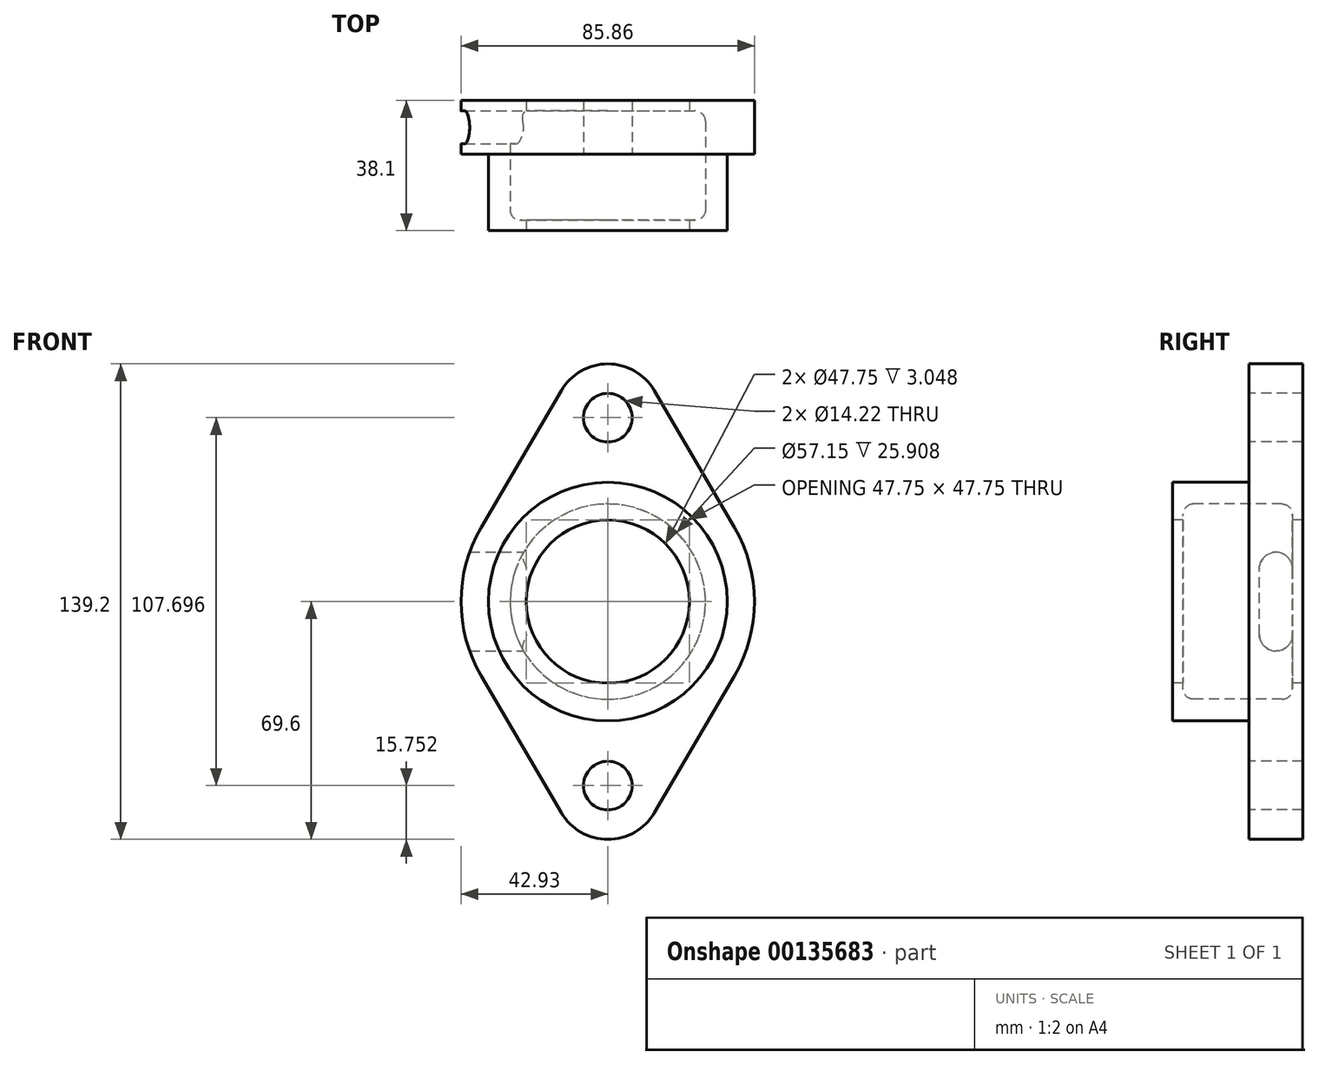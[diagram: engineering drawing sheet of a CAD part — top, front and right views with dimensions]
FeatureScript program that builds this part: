
annotation { "Feature Type Name" : "Feature", "Feature Type Description" : "" }
export const myFeature = defineFeature(function(context is Context, id is Id, definition is map)
    precondition{}
    {
        {
            var Q0;
            Q0=qCreatedBy(makeId("Front.planeOp"),FACE);
            var sketch = newSketch(context, id + "F0", { "sketchPlane" : qUnion([Q0])});
            skArc(sketch, "E0", {"start": v(37.06, -21.67) * mm, "mid": v(42.93, 0) * mm, "end": v(37.06, 21.67) * mm});
            skArc(sketch, "E1", {"start": v(-37.06, 21.67) * mm, "mid": v(-42.93, 0) * mm, "end": v(-37.06, -21.67) * mm});
            skLineSegment(sketch, "E2", {"start": v(-37.06, 21.67) * mm, "end": v(-13.6, 61.8) * mm});
            skLineSegment(sketch, "E3", {"start": v(-37.06, -21.67) * mm, "end": v(-13.6, -61.8) * mm});
            skLineSegment(sketch, "E4", {"start": v(37.06, 21.67) * mm, "end": v(13.6, 61.8) * mm});
            skLineSegment(sketch, "E5", {"start": v(37.06, -21.67) * mm, "end": v(13.6, -61.8) * mm});
            skArc(sketch, "E6", {"start": v(13.6, 61.8) * mm, "mid": v(0, 69.6) * mm, "end": v(-13.6, 61.8) * mm});
            skArc(sketch, "E7", {"start": v(-13.6, -61.8) * mm, "mid": v(0, -69.6) * mm, "end": v(13.6, -61.8) * mm});
            skCircle(sketch, "E8", {"center": v(0, 53.85) * mm, "radius": 7.11 * mm});
            skCircle(sketch, "E9", {"center": v(0, -53.85) * mm, "radius": 7.11 * mm});
            skSolve(sketch);
        }
        {
            var Q0;
            Q0=qSketchRegion(id+"F0",true);
            extrude(context, id + "F1", {"entities" : qUnion([Q0]), "oppositeDirection" : true, "depth" : 15.75 * mm});
        }
        {
            var Q0;
            Q0=makeQuery(id+"F1.opExtrude","CAP_FACE",FACE,{"disambiguationData":[OSD([sQuery(id+"F0.wireOp",EDGE,"E0"),sQuery(id+"F0.wireOp",EDGE,"E1"),sQuery(id+"F0.wireOp",EDGE,"E2"),sQuery(id+"F0.wireOp",EDGE,"E3"),sQuery(id+"F0.wireOp",EDGE,"E4"),sQuery(id+"F0.wireOp",EDGE,"E5"),sQuery(id+"F0.wireOp",EDGE,"E6"),sQuery(id+"F0.wireOp",EDGE,"E7"),sQuery(id+"F0.wireOp",EDGE,"E8"),sQuery(id+"F0.wireOp",EDGE,"E9")])],"isStart":true});
            var sketch = newSketch(context, id + "F2", { "sketchPlane" : qUnion([Q0])});
            skCircle(sketch, "E10", {"center": v(0, 0) * mm, "radius": 34.93 * mm});
            skSolve(sketch);
        }
        {
            var Q0;
            Q0=qSketchRegion(id+"F2",true);
            extrude(context, id + "F3", {"entities" : qUnion([Q0]), "operationType" : NewBodyOperationType.ADD, "depth" : 22.35 * mm});
        }
        {
            var Q0;
            Q0=qCreatedBy(makeId("Top.planeOp"),FACE);
            var sketch = newSketch(context, id + "F4", { "sketchPlane" : qUnion([Q0])});
            skLineSegment(sketch, "E11.bottom", {"start": v(-25.53, 12.7) * mm, "end": v(0, 12.7) * mm});
            skLineSegment(sketch, "E11.top", {"start": v(-25.53, -19.3) * mm, "end": v(0, -19.3) * mm});
            skLineSegment(sketch, "E11.left", {"start": v(-28.57, 9.65) * mm, "end": v(-28.57, -16.26) * mm});
            skPoint(sketch, "E12.visualSharp", {"position": v(-28.57, 12.7) * mm});
            skArc(sketch, "E12.filletArc", {"start": v(-25.53, 12.7) * mm, "mid": v(-27.68, 11.8) * mm, "end": v(-28.58, 9.65) * mm});
            skPoint(sketch, "E13.visualSharp", {"position": v(-28.57, -19.3) * mm});
            skArc(sketch, "E13.filletArc", {"start": v(-28.57, -16.26) * mm, "mid": v(-27.68, -18.41) * mm, "end": v(-25.53, -19.3) * mm});
            skLineSegment(sketch, "E14", {"start": v(0, 12.7) * mm, "end": v(0, -19.3) * mm});
            skLineSegment(sketch, "E15", {"start": v(0, 31.56) * mm, "end": v(0, -35.77) * mm, "construction": true});
            skSolve(sketch);
        }
        {
            var Q0;
            Q0=makeQuery(id+"F3.opExtrude","CAP_FACE",FACE,{"disambiguationData":[OSD([sQuery(id+"F2.wireOp",EDGE,"E10")])],"isStart":false});
            var sketch = newSketch(context, id + "F5", { "sketchPlane" : qUnion([Q0])});
            skCircle(sketch, "E16", {"center": v(0, 0) * mm, "radius": 23.88 * mm});
            skSolve(sketch);
        }
        {
            var Q0;
            Q0=qSketchRegion(id+"F5",true);
            extrude(context, id + "F6", {"entities" : qUnion([Q0]), "operationType" : NewBodyOperationType.REMOVE, "endBound" : BoundingType.THROUGH_ALL, "oppositeDirection" : true, "depth" : 25.4 * mm});
        }
        {
            var Q0;
            Q0=qSketchRegion(id+"F4",true);
            var Q1;
            Q1=sQuery(id+"F4.wireOp",EDGE,"E15");
            revolve(context, id + "F7", {"operationType" : NewBodyOperationType.REMOVE, "entities" : qUnion([Q0]), "axis" : qUnion([Q1]), "revolveType" : RevolveType.FULL, "oppositeDirection" : true});
        }
        {
            var Q0;
            Q0=qCreatedBy(makeId("Right.planeOp"),FACE);
            var sketch = newSketch(context, id + "F8", { "sketchPlane" : qUnion([Q0])});
            skLineSegment(sketch, "E17", {"start": v(50.09, 0) * mm, "end": v(-60.9, 0) * mm, "construction": true});
            skLineSegment(sketch, "E18", {"start": v(12.7, 9.65) * mm, "end": v(12.7, -9.65) * mm});
            skArc(sketch, "E19", {"start": v(12.7, 9.65) * mm, "mid": v(7.87, 14.48) * mm, "end": v(3.05, 9.65) * mm});
            skArc(sketch, "E20", {"start": v(3.05, -9.65) * mm, "mid": v(7.87, -14.48) * mm, "end": v(12.7, -9.65) * mm});
            skLineSegment(sketch, "E21", {"start": v(3.05, -9.65) * mm, "end": v(3.05, 9.65) * mm});
            skSolve(sketch);
        }
        {
            var Q0;
            Q0=qSketchRegion(id+"F8",true);
            extrude(context, id + "F9", {"entities" : qUnion([Q0]), "operationType" : NewBodyOperationType.REMOVE, "endBound" : BoundingType.THROUGH_ALL, "oppositeDirection" : true, "depth" : 25.4 * mm});
        }
    });
